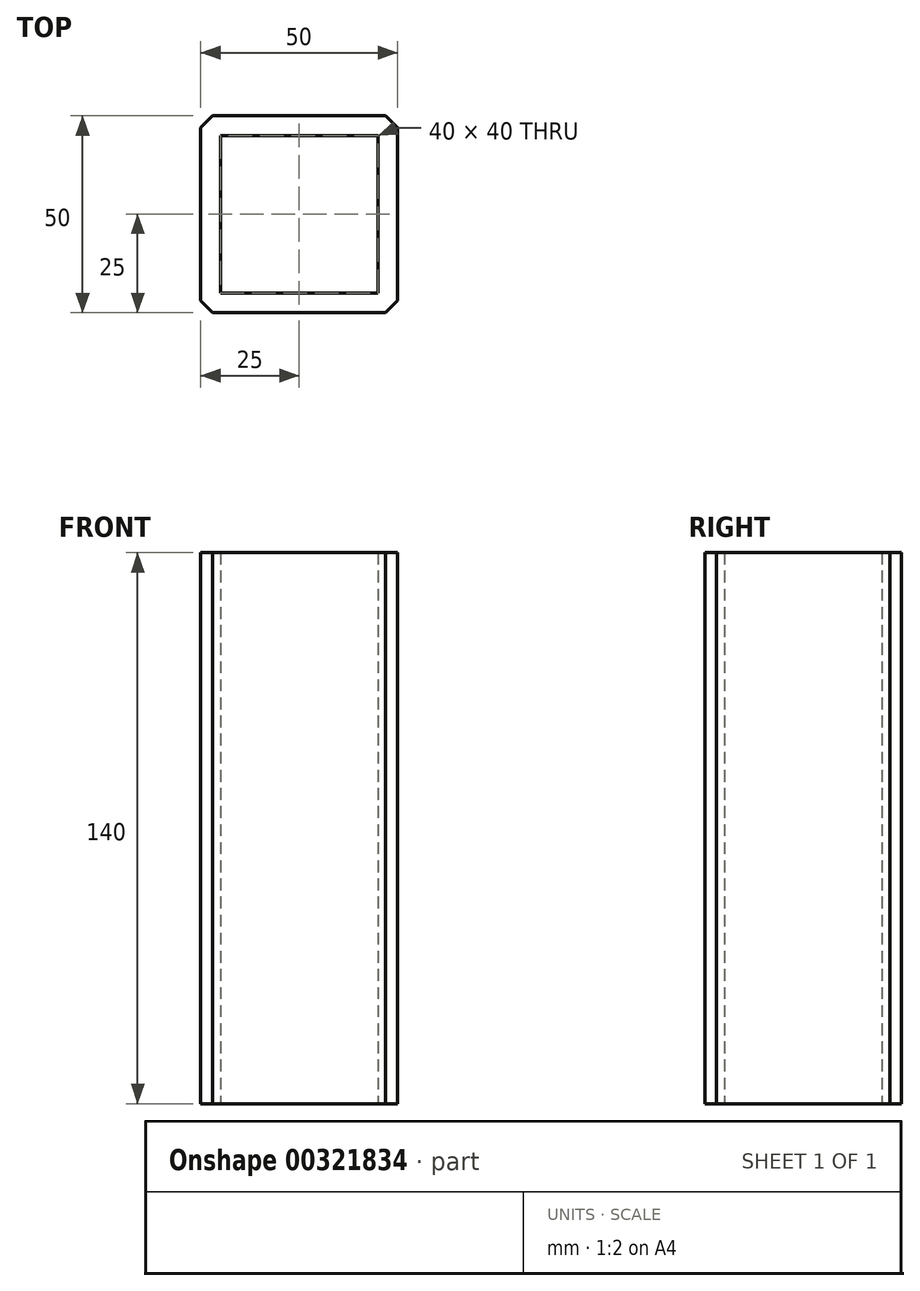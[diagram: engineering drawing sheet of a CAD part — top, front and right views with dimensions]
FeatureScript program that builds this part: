
annotation { "Feature Type Name" : "Feature", "Feature Type Description" : "" }
export const myFeature = defineFeature(function(context is Context, id is Id, definition is map)
    precondition{}
    {
        {
            var Q0;
            Q0=qCreatedBy(makeId("Top.planeOp"),FACE);
            var sketch = newSketch(context, id + "F0", { "sketchPlane" : qUnion([Q0])});
            skLineSegment(sketch, "E0.bottom", {"start": v(-25, 25) * mm, "end": v(25, 25) * mm});
            skLineSegment(sketch, "E0.top", {"start": v(-25, -25) * mm, "end": v(25, -25) * mm});
            skLineSegment(sketch, "E0.left", {"start": v(-25, 25) * mm, "end": v(-25, -25) * mm});
            skLineSegment(sketch, "E0.right", {"start": v(25, 25) * mm, "end": v(25, -25) * mm});
            skLineSegment(sketch, "E1.0", {"start": v(-20, 20) * mm, "end": v(20, 20) * mm});
            skLineSegment(sketch, "E1.1", {"start": v(-20, 20) * mm, "end": v(-20, -20) * mm});
            skLineSegment(sketch, "E1.2", {"start": v(-20, -20) * mm, "end": v(20, -20) * mm});
            skLineSegment(sketch, "E1.3", {"start": v(20, 20) * mm, "end": v(20, -20) * mm});
            skSolve(sketch);
        }
        {
            var Q0;
            Q0 = qSketchRegion(id + "F0", true);
            extrude(context, id + "F1", {"entities" : qUnion([Q0]), "depth" : 140 * mm});
        }
        {
            var Q0;
            Q0=makeQuery(id+"F1.opExtrude","SWEPT_EDGE",EDGE,{"disambiguationData":[OSD([sQuery(id+"F0.wireOp",EDGE,"E0.top"),sQuery(id+"F0.wireOp",EDGE,"E0.right")])]});
            var Q1;
            Q1=makeQuery(id+"F1.opExtrude","SWEPT_EDGE",EDGE,{"disambiguationData":[OSD([sQuery(id+"F0.wireOp",EDGE,"E0.top"),sQuery(id+"F0.wireOp",EDGE,"E0.left")])]});
            var Q2;
            Q2=makeQuery(id+"F1.opExtrude","SWEPT_EDGE",EDGE,{"disambiguationData":[OSD([sQuery(id+"F0.wireOp",EDGE,"E0.bottom"),sQuery(id+"F0.wireOp",EDGE,"E0.right")])]});
            var Q3;
            Q3=makeQuery(id+"F1.opExtrude","SWEPT_EDGE",EDGE,{"disambiguationData":[OSD([sQuery(id+"F0.wireOp",EDGE,"E0.bottom"),sQuery(id+"F0.wireOp",EDGE,"E0.left")])]});
            chamfer(context, id + "F2", {"entities" : qUnion([Q0, Q1, Q2, Q3]), "width" : 3 * mm, "tangentPropagation" : true});
        }
    });
